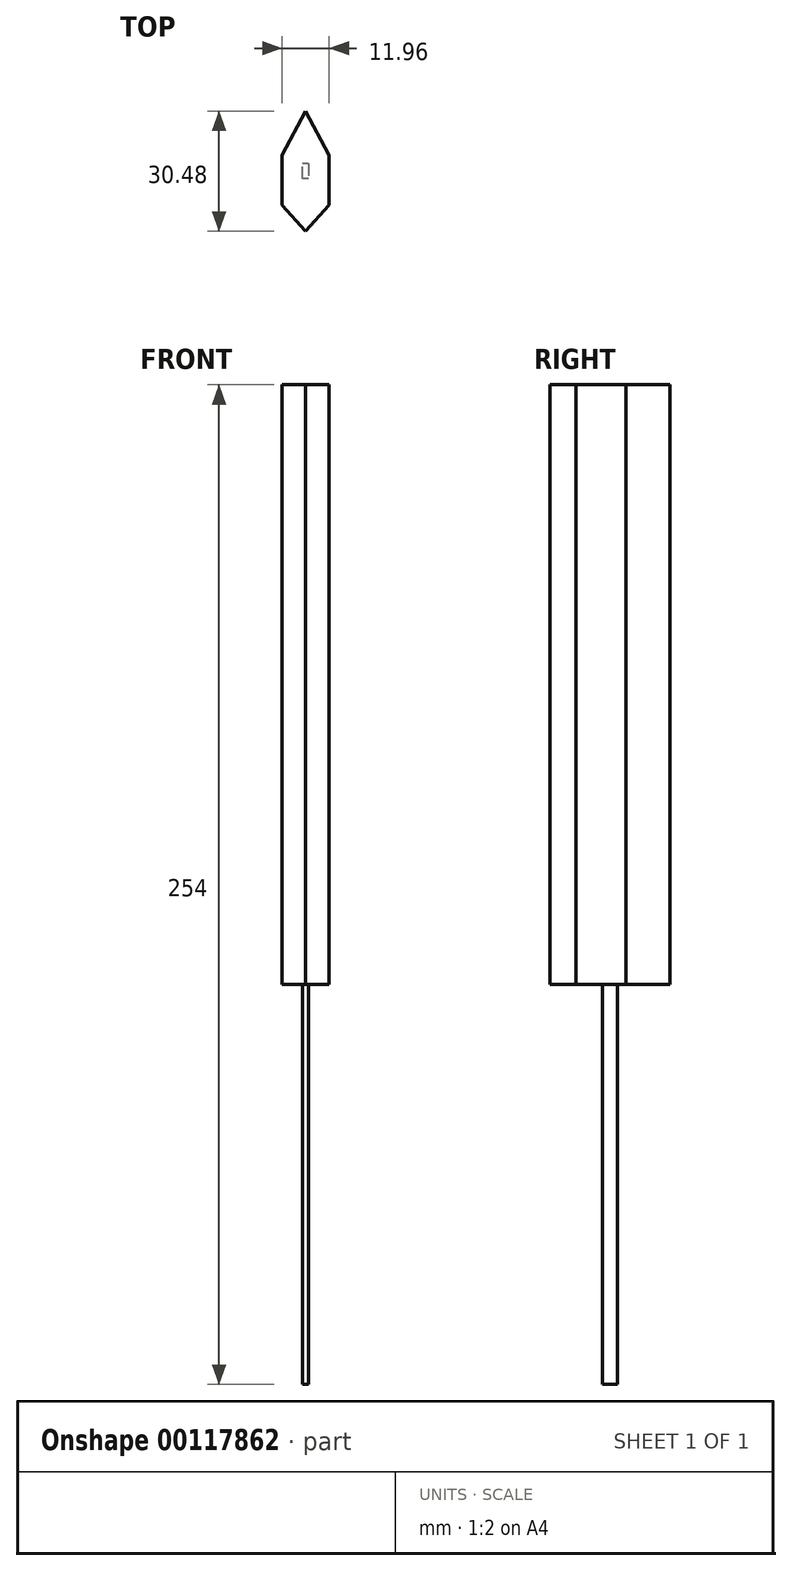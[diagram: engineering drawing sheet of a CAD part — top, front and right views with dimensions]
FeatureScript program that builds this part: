
annotation { "Feature Type Name" : "Feature", "Feature Type Description" : "" }
export const myFeature = defineFeature(function(context is Context, id is Id, definition is map)
    precondition{}
    {
        {
            var Q0;
            Q0=qCreatedBy(makeId("Top.planeOp"),FACE);
            var sketch = newSketch(context, id + "F0", { "sketchPlane" : qUnion([Q0])});
            skLineSegment(sketch, "E0", {"start": v(-5.98, -23.9) * mm, "end": v(-5.98, -11.2) * mm});
            skLineSegment(sketch, "E1", {"start": v(-5.98, -23.9) * mm, "end": v(0, -30.48) * mm});
            skLineSegment(sketch, "E2", {"start": v(0, -30.48) * mm, "end": v(0, 0) * mm});
            skLineSegment(sketch, "E3", {"start": v(0, 0) * mm, "end": v(-5.98, -11.2) * mm});
            skLineSegment(sketch, "E4", {"start": v(0, -30.48) * mm, "end": v(-5.98, -23.9) * mm});
            skLineSegment(sketch, "E5", {"start": v(-5.98, -11.2) * mm, "end": v(0, 0) * mm});
            skLineSegment(sketch, "E6.MirrorCS", {"start": v(0, -30.48) * mm, "end": v(5.98, -23.9) * mm});
            skLineSegment(sketch, "E7.MirrorCS", {"start": v(5.98, -23.9) * mm, "end": v(5.98, -11.2) * mm});
            skLineSegment(sketch, "E8.MirrorCS", {"start": v(5.98, -11.2) * mm, "end": v(0, 0) * mm});
            skSolve(sketch);
        }
        {
            var Q0;
            Q0 = qSketchRegion(id + "F0", true);
            extrude(context, id + "F1", {"entities" : qUnion([Q0]), "endBound" : BoundingType.SYMMETRIC, "depth" : 152.4 * mm});
        }
        {
            var Q0;
            Q0=makeQuery(id+"F1.opExtrude","CAP_FACE",FACE,{"disambiguationData":[OSD([sQuery(id+"F0.wireOp",EDGE,"E0"),sQuery(id+"F0.wireOp",EDGE,"E4"),sQuery(id+"F0.wireOp",EDGE,"E5"),sQuery(id+"F0.wireOp",EDGE,"E6.MirrorCS"),sQuery(id+"F0.wireOp",EDGE,"E7.MirrorCS"),sQuery(id+"F0.wireOp",EDGE,"E8.MirrorCS")])],"isStart":true});
            var sketch = newSketch(context, id + "F2", { "sketchPlane" : qUnion([Q0])});
            skLineSegment(sketch, "E9", {"start": v(0, 30.48) * mm, "end": v(0, 0) * mm});
            skLineSegment(sketch, "E10", {"start": v(0, 0) * mm, "end": v(0, 15.24) * mm});
            skLineSegment(sketch, "E11", {"start": v(0, 15.24) * mm, "end": v(0, 17.14) * mm});
            skLineSegment(sketch, "E12", {"start": v(0, 17.14) * mm, "end": v(-0.76, 17.14) * mm});
            skLineSegment(sketch, "E13.bottom", {"start": v(-0.76, 17.14) * mm, "end": v(0, 17.14) * mm});
            skLineSegment(sketch, "E13.top", {"start": v(-0.76, 15.24) * mm, "end": v(0, 15.24) * mm});
            skLineSegment(sketch, "E13.left", {"start": v(-0.76, 17.14) * mm, "end": v(-0.76, 15.24) * mm});
            skLineSegment(sketch, "E13.right", {"start": v(0, 17.14) * mm, "end": v(0, 15.24) * mm});
            skLineSegment(sketch, "E14.MirrorCS", {"start": v(-0.76, 13.34) * mm, "end": v(-0.76, 15.24) * mm});
            skLineSegment(sketch, "E15.MirrorCS", {"start": v(-0.76, 13.34) * mm, "end": v(0, 13.34) * mm});
            skLineSegment(sketch, "E16.MirrorCS", {"start": v(0.76, 17.14) * mm, "end": v(0.76, 15.24) * mm});
            skLineSegment(sketch, "E17.MirrorCS", {"start": v(0.76, 13.34) * mm, "end": v(0.76, 15.24) * mm});
            skLineSegment(sketch, "E18.MirrorCS", {"start": v(0.76, 17.14) * mm, "end": v(0, 17.14) * mm});
            skLineSegment(sketch, "E19.MirrorCS", {"start": v(0.76, 13.34) * mm, "end": v(0, 13.34) * mm});
            skSolve(sketch);
        }
        {
            var Q0;
            Q0 = qSketchRegion(id + "F2", true);
            extrude(context, id + "F3", {"entities" : qUnion([Q0]), "operationType" : NewBodyOperationType.ADD, "depth" : 101.6 * mm});
        }
    });
